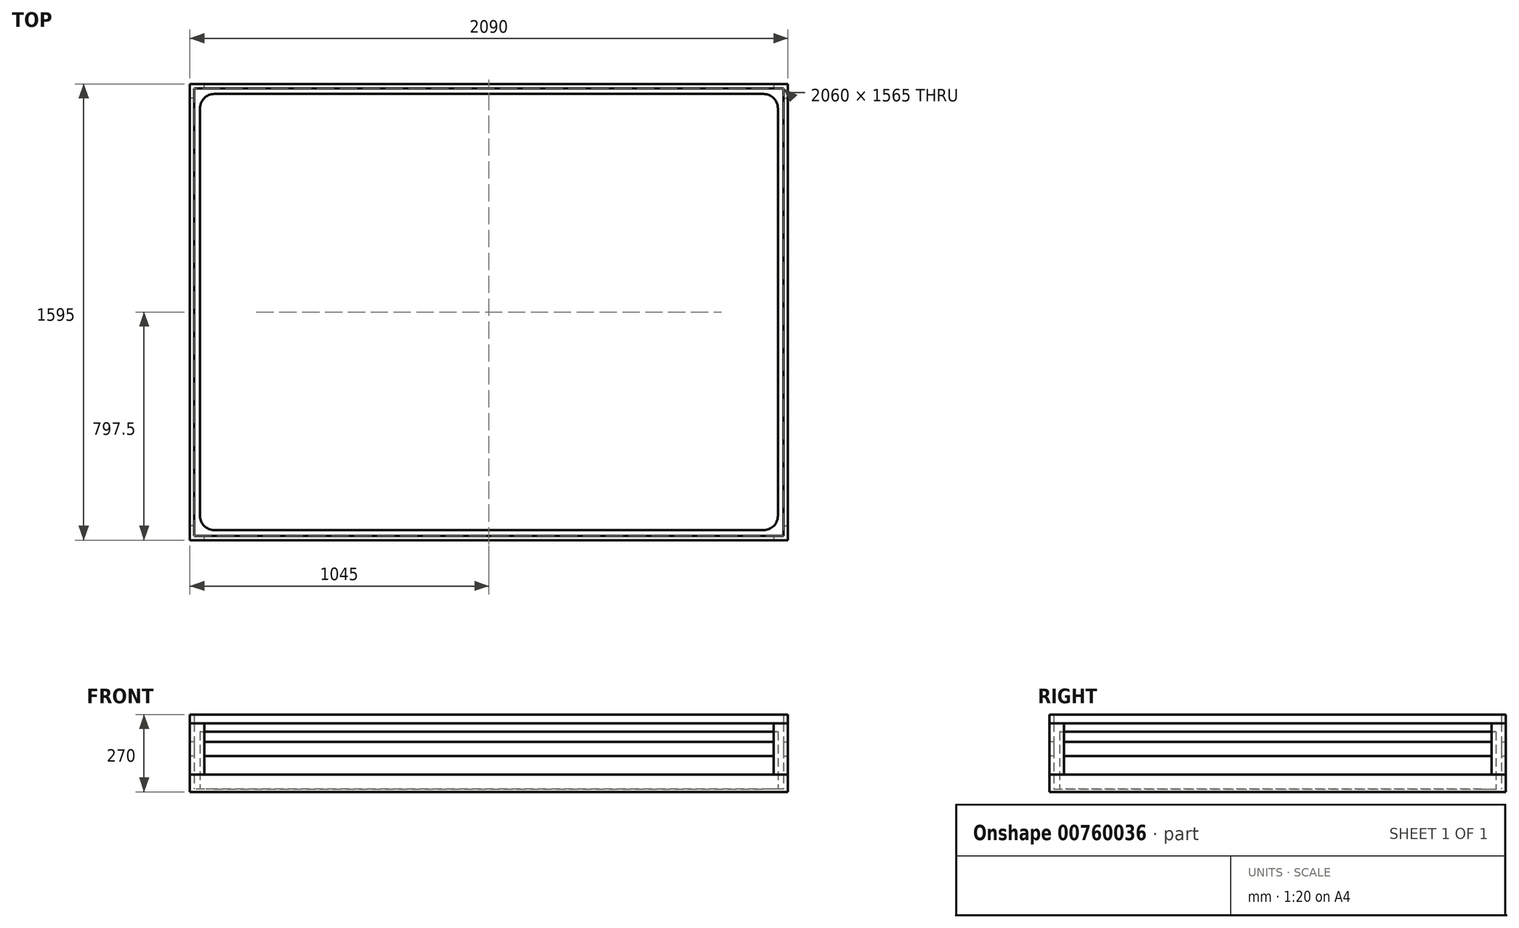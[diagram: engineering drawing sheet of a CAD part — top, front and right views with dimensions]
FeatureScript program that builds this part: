
annotation { "Feature Type Name" : "Feature", "Feature Type Description" : "" }
export const myFeature = defineFeature(function(context is Context, id is Id, definition is map)
    precondition{}
    {
        {
            var Q0;
            Q0=qCreatedBy(makeId("Top.planeOp"),FACE);
            var sketch = newSketch(context, id + "F0", { "sketchPlane" : qUnion([Q0])});
            skLineSegment(sketch, "E0.bottom", {"start": v(-1010, 762.5) * mm, "end": v(1010, 762.5) * mm});
            skLineSegment(sketch, "E0.top", {"start": v(-1010, -762.5) * mm, "end": v(1010, -762.5) * mm});
            skLineSegment(sketch, "E0.left", {"start": v(-1010, 762.5) * mm, "end": v(-1010, -762.5) * mm});
            skLineSegment(sketch, "E0.right", {"start": v(1010, 762.5) * mm, "end": v(1010, -762.5) * mm});
            skPoint(sketch, "E1", {"position": v(0, 0) * mm});
            skSolve(sketch);
        }
        {
            var Q0;
            Q0=makeQuery(id+"F0.imprint","IMPRINT",FACE,{"disambiguationData":[TD([[makeQuery(id+"F0.imprint","IMPRINT",EDGE,{"derivedFrom":sQuery(id+"F0.wireOp",EDGE,"E0.bottom")}),-1.0]])]});
            extrude(context, id + "F1", {"entities" : qUnion([Q0]), "depth" : 200 * mm, "offsetDistance" : 25 * mm});
        }
        {
            var Q0;
            Q0=makeQuery(id+"F1.opExtrude","SWEPT_EDGE",EDGE,{"disambiguationData":[OSD([sQuery(id+"F0.wireOp",EDGE,"E0.top"),sQuery(id+"F0.wireOp",EDGE,"E0.right")])]});
            var Q1;
            Q1=makeQuery(id+"F1.opExtrude","SWEPT_EDGE",EDGE,{"disambiguationData":[OSD([sQuery(id+"F0.wireOp",EDGE,"E0.top"),sQuery(id+"F0.wireOp",EDGE,"E0.left")])]});
            var Q2;
            Q2=makeQuery(id+"F1.opExtrude","SWEPT_EDGE",EDGE,{"disambiguationData":[OSD([sQuery(id+"F0.wireOp",EDGE,"E0.bottom"),sQuery(id+"F0.wireOp",EDGE,"E0.left")])]});
            var Q3;
            Q3=makeQuery(id+"F1.opExtrude","SWEPT_EDGE",EDGE,{"disambiguationData":[OSD([sQuery(id+"F0.wireOp",EDGE,"E0.bottom"),sQuery(id+"F0.wireOp",EDGE,"E0.right")])]});
            fillet(context, id + "F2", {"entities" : qUnion([Q0, Q1, Q2, Q3]), "radius" : 50 * mm, "tangentPropagation" : true, "allowEdgeOverflow" : false});
        }
        {
            var Q0;
            Q0=qCreatedBy(makeId("Top.planeOp"),FACE);
            var sketch = newSketch(context, id + "F3", { "sketchPlane" : qUnion([Q0])});
            skLineSegment(sketch, "E2.0", {"start": v(-1030, 782.5) * mm, "end": v(-1030, -782.5) * mm});
            skLineSegment(sketch, "E2.1", {"start": v(1030, 782.5) * mm, "end": v(-1030, 782.5) * mm});
            skLineSegment(sketch, "E2.2", {"start": v(1030, -782.5) * mm, "end": v(1030, 782.5) * mm});
            skLineSegment(sketch, "E2.3", {"start": v(-1030, -782.5) * mm, "end": v(1030, -782.5) * mm});
            skSolve(sketch);
        }
        {
            var Q0;
            Q0=makeQuery(id+"F3.imprint","IMPRINT",FACE,{"disambiguationData":[TD([[makeQuery(id+"F3.imprint","IMPRINT",EDGE,{"derivedFrom":sQuery(id+"F3.wireOp",EDGE,"E2.0")}),1.0]])]});
            var sketch = newSketch(context, id + "F4", { "sketchPlane" : qUnion([Q0])});
            skLineSegment(sketch, "E3.0", {"start": v(-1045, 797.5) * mm, "end": v(-1045, -797.5) * mm});
            skLineSegment(sketch, "E3.1", {"start": v(1045, 797.5) * mm, "end": v(-1045, 797.5) * mm});
            skLineSegment(sketch, "E3.2", {"start": v(1045, -797.5) * mm, "end": v(1045, 797.5) * mm});
            skLineSegment(sketch, "E3.3", {"start": v(-1045, -797.5) * mm, "end": v(1045, -797.5) * mm});
            skSolve(sketch);
        }
        {
            var Q0;
            Q0=makeQuery(id+"F4.imprint","IMPRINT",FACE,{"disambiguationData":[TD([[makeQuery(id+"F4.imprint","IMPRINT",EDGE,{"derivedFrom":sQuery(id+"F4.wireOp",EDGE,"E3.0")}),1.0]])]});
            extrude(context, id + "F5", {"entities" : qUnion([Q0]), "depth" : 50 * mm, "offsetDistance" : 25 * mm});
        }
        {
            var Q0;
            Q0=qCreatedBy(makeId("Top.planeOp"),FACE);
            var sketch = newSketch(context, id + "F6", { "sketchPlane" : qUnion([Q0])});
            skLineSegment(sketch, "E4.bottom", {"start": v(1045, -797.5) * mm, "end": v(-1045, -797.5) * mm});
            skLineSegment(sketch, "E4.top", {"start": v(1045, 797.5) * mm, "end": v(-1045, 797.5) * mm});
            skLineSegment(sketch, "E4.left", {"start": v(1045, -797.5) * mm, "end": v(1045, 797.5) * mm});
            skLineSegment(sketch, "E4.right", {"start": v(-1045, -797.5) * mm, "end": v(-1045, 797.5) * mm});
            skSolve(sketch);
        }
        {
            var Q0;
            Q0=makeQuery(id+"F6.imprint","IMPRINT",FACE,{"disambiguationData":[TD([[makeQuery(id+"F6.imprint","IMPRINT",EDGE,{"derivedFrom":sQuery(id+"F6.wireOp",EDGE,"E4.bottom")}),-1.0]])]});
            extrude(context, id + "F7", {"entities" : qUnion([Q0]), "operationType" : NewBodyOperationType.ADD, "oppositeDirection" : true, "depth" : 10 * mm, "offsetDistance" : 25 * mm});
        }
        {
            var Q0;
            Q0=makeQuery(id+"F5.opExtrude","CAP_FACE",FACE,{"disambiguationData":[OSD([sQuery(id+"F3.wireOp",EDGE,"E2.0"),sQuery(id+"F3.wireOp",EDGE,"E2.1"),sQuery(id+"F3.wireOp",EDGE,"E2.2"),sQuery(id+"F3.wireOp",EDGE,"E2.3"),sQuery(id+"F4.wireOp",EDGE,"E3.0"),sQuery(id+"F4.wireOp",EDGE,"E3.1"),sQuery(id+"F4.wireOp",EDGE,"E3.2"),sQuery(id+"F4.wireOp",EDGE,"E3.3")])],"isStart":false});
            cPlane(context, id + "F8", {"entities" : qUnion([Q0]), "cplaneType" : CPlaneType.OFFSET, "offset" : 180 * mm, "width" : 150 * mm, "height" : 150 * mm});
        }
        {
            var Q0;
            Q0=qCreatedBy(id+"F8.planeOp",FACE);
            var sketch = newSketch(context, id + "F9", { "sketchPlane" : qUnion([Q0])});
            skLineSegment(sketch, "E5.bottom", {"start": v(-1045, 797.5) * mm, "end": v(1045, 797.5) * mm});
            skLineSegment(sketch, "E5.top", {"start": v(-1045, -797.5) * mm, "end": v(1045, -797.5) * mm});
            skLineSegment(sketch, "E5.left", {"start": v(-1045, 797.5) * mm, "end": v(-1045, -797.5) * mm});
            skLineSegment(sketch, "E5.right", {"start": v(1045, 797.5) * mm, "end": v(1045, -797.5) * mm});
            skLineSegment(sketch, "E6.0", {"start": v(-1030, 782.5) * mm, "end": v(-1030, -782.5) * mm});
            skLineSegment(sketch, "E6.1", {"start": v(-1030, 782.5) * mm, "end": v(1030, 782.5) * mm});
            skLineSegment(sketch, "E6.2", {"start": v(1030, 782.5) * mm, "end": v(1030, -782.5) * mm});
            skLineSegment(sketch, "E6.3", {"start": v(-1030, -782.5) * mm, "end": v(1030, -782.5) * mm});
            skSolve(sketch);
        }
        {
            var Q0;
            Q0=makeQuery(id+"F9.imprint","IMPRINT",FACE,{"disambiguationData":[TD([[makeQuery(id+"F9.imprint","IMPRINT",EDGE,{"derivedFrom":sQuery(id+"F9.wireOp",EDGE,"E5.bottom")}),-1.0]])]});
            extrude(context, id + "F10", {"entities" : qUnion([Q0]), "depth" : 30 * mm, "offsetDistance" : 25 * mm});
        }
        {
            var Q0;
            Q0=makeQuery(id+"F5.opExtrude","CAP_FACE",FACE,{"disambiguationData":[OSD([sQuery(id+"F3.wireOp",EDGE,"E2.0"),sQuery(id+"F3.wireOp",EDGE,"E2.1"),sQuery(id+"F3.wireOp",EDGE,"E2.2"),sQuery(id+"F3.wireOp",EDGE,"E2.3"),sQuery(id+"F4.wireOp",EDGE,"E3.0"),sQuery(id+"F4.wireOp",EDGE,"E3.1"),sQuery(id+"F4.wireOp",EDGE,"E3.2"),sQuery(id+"F4.wireOp",EDGE,"E3.3")])],"isStart":false});
            cPlane(context, id + "F11", {"entities" : qUnion([Q0]), "cplaneType" : CPlaneType.OFFSET, "offset" : 0 * mm, "width" : 150 * mm, "height" : 150 * mm});
        }
        {
            var Q0;
            Q0=qCreatedBy(id+"F11.planeOp",FACE);
            var sketch = newSketch(context, id + "F12", { "sketchPlane" : qUnion([Q0])});
            skLineSegment(sketch, "E7", {"start": v(-1045, -747.5) * mm, "end": v(-1045, -797.5) * mm});
            skLineSegment(sketch, "E8", {"start": v(-1045, -797.5) * mm, "end": v(-995, -797.5) * mm});
            skLineSegment(sketch, "E9", {"start": v(-995, -797.5) * mm, "end": v(-995, -782.5) * mm});
            skLineSegment(sketch, "E10", {"start": v(-995, -782.5) * mm, "end": v(-1030, -782.5) * mm});
            skLineSegment(sketch, "E11", {"start": v(-1030, -782.5) * mm, "end": v(-1030, -747.5) * mm});
            skLineSegment(sketch, "E12", {"start": v(-1030, -747.5) * mm, "end": v(-1045, -747.5) * mm});
            skSolve(sketch);
        }
        {
            var Q0;
            Q0=makeQuery(id+"F12.imprint","IMPRINT",FACE,{"disambiguationData":[TD([[makeQuery(id+"F12.imprint","IMPRINT",EDGE,{"derivedFrom":sQuery(id+"F12.wireOp",EDGE,"E7")}),1.0]])]});
            extrude(context, id + "F13", {"entities" : qUnion([Q0]), "depth" : 180 * mm, "offsetDistance" : 25 * mm});
        }
        {
            var Q0;
            Q0=makeQuery(id+"F13.opExtrude","SWEPT_BODY",BODY,{"disambiguationData":[OSD([sQuery(id+"F12.wireOp",EDGE,"E7"),sQuery(id+"F12.wireOp",EDGE,"E8"),sQuery(id+"F12.wireOp",EDGE,"E9"),sQuery(id+"F12.wireOp",EDGE,"E10"),sQuery(id+"F12.wireOp",EDGE,"E11"),sQuery(id+"F12.wireOp",EDGE,"E12")])]});
            var Q1;
            Q1=qCreatedBy(makeId("Front.planeOp"),FACE);
            mirror(context, id + "F14", {"entities" : qUnion([Q0]), "mirrorPlane" : qUnion([Q1])});
        }
        {
            var Q0;
            Q0=makeQuery(id+"F13.opExtrude","SWEPT_BODY",BODY,{"disambiguationData":[OSD([sQuery(id+"F12.wireOp",EDGE,"E7"),sQuery(id+"F12.wireOp",EDGE,"E8"),sQuery(id+"F12.wireOp",EDGE,"E9"),sQuery(id+"F12.wireOp",EDGE,"E10"),sQuery(id+"F12.wireOp",EDGE,"E11"),sQuery(id+"F12.wireOp",EDGE,"E12")])]});
            var Q1;
            Q1=makeQuery(id+"F14.opPattern","COPY",BODY,{"derivedFrom":makeQuery(id+"F13.opExtrude","SWEPT_BODY",BODY,{"disambiguationData":[OSD([sQuery(id+"F12.wireOp",EDGE,"E7"),sQuery(id+"F12.wireOp",EDGE,"E8"),sQuery(id+"F12.wireOp",EDGE,"E9"),sQuery(id+"F12.wireOp",EDGE,"E10"),sQuery(id+"F12.wireOp",EDGE,"E11"),sQuery(id+"F12.wireOp",EDGE,"E12")])]}),"instanceName":"1"});
            var Q2;
            Q2=qCreatedBy(makeId("Right.planeOp"),FACE);
            mirror(context, id + "F15", {"entities" : qUnion([Q0, Q1]), "mirrorPlane" : qUnion([Q2])});
        }
        {
            var Q0;
            Q0=makeQuery(id+"F15.opPattern","COPY",FACE,{"derivedFrom":makeQuery(id+"F13.opExtrude","SWEPT_FACE",FACE,{"disambiguationData":[OSD([sQuery(id+"F12.wireOp",EDGE,"E9")])]}),"instanceName":"1"});
            var sketch = newSketch(context, id + "F16", { "sketchPlane" : qUnion([Q0])});
            skLineSegment(sketch, "E13.bottom", {"start": v(782.5, 165) * mm, "end": v(797.5, 165) * mm});
            skLineSegment(sketch, "E13.top", {"start": v(782.5, 115) * mm, "end": v(797.5, 115) * mm});
            skLineSegment(sketch, "E13.left", {"start": v(782.5, 165) * mm, "end": v(782.5, 115) * mm});
            skLineSegment(sketch, "E13.right", {"start": v(797.5, 165) * mm, "end": v(797.5, 115) * mm});
            skSolve(sketch);
        }
        {
            var Q0;
            Q0=makeQuery(id+"F16.imprint","IMPRINT",FACE,{"disambiguationData":[TD([[makeQuery(id+"F16.imprint","IMPRINT",EDGE,{"derivedFrom":sQuery(id+"F16.wireOp",EDGE,"E13.bottom")}),-1.0]])]});
            extrude(context, id + "F17", {"entities" : qUnion([Q0]), "depth" : 1990 * mm, "offsetDistance" : 25 * mm});
        }
        {
            var Q0;
            Q0=makeQuery(id+"F13.opExtrude","SWEPT_FACE",FACE,{"disambiguationData":[OSD([sQuery(id+"F12.wireOp",EDGE,"E12")])]});
            var sketch = newSketch(context, id + "F18", { "sketchPlane" : qUnion([Q0])});
            skLineSegment(sketch, "E14.bottom", {"start": v(1030, 165) * mm, "end": v(1045, 165) * mm});
            skLineSegment(sketch, "E14.top", {"start": v(1030, 115) * mm, "end": v(1045, 115) * mm});
            skLineSegment(sketch, "E14.left", {"start": v(1030, 165) * mm, "end": v(1030, 115) * mm});
            skLineSegment(sketch, "E14.right", {"start": v(1045, 165) * mm, "end": v(1045, 115) * mm});
            skSolve(sketch);
        }
        {
            var Q0;
            Q0=makeQuery(id+"F18.imprint","IMPRINT",FACE,{"disambiguationData":[TD([[makeQuery(id+"F18.imprint","IMPRINT",EDGE,{"derivedFrom":sQuery(id+"F18.wireOp",EDGE,"E14.bottom")}),-1.0]])]});
            extrude(context, id + "F19", {"entities" : qUnion([Q0]), "depth" : 1495 * mm, "offsetDistance" : 25 * mm});
        }
        {
            var Q0;
            Q0=makeQuery(id+"F19.opExtrude","SWEPT_BODY",BODY,{"disambiguationData":[OSD([sQuery(id+"F18.wireOp",EDGE,"E14.bottom"),sQuery(id+"F18.wireOp",EDGE,"E14.top"),sQuery(id+"F18.wireOp",EDGE,"E14.left"),sQuery(id+"F18.wireOp",EDGE,"E14.right")])]});
            var Q1;
            Q1=qCreatedBy(makeId("Right.planeOp"),FACE);
            mirror(context, id + "F20", {"entities" : qUnion([Q0]), "mirrorPlane" : qUnion([Q1])});
        }
        {
            var Q0;
            Q0=makeQuery(id+"F17.opExtrude","SWEPT_BODY",BODY,{"disambiguationData":[OSD([sQuery(id+"F16.wireOp",EDGE,"E13.bottom"),sQuery(id+"F16.wireOp",EDGE,"E13.top"),sQuery(id+"F16.wireOp",EDGE,"E13.left"),sQuery(id+"F16.wireOp",EDGE,"E13.right")])]});
            var Q1;
            Q1=qCreatedBy(makeId("Front.planeOp"),FACE);
            mirror(context, id + "F21", {"entities" : qUnion([Q0]), "mirrorPlane" : qUnion([Q1])});
        }
    });
